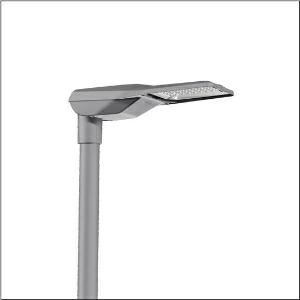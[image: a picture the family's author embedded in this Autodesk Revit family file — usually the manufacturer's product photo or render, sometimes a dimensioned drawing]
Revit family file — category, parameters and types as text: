
# Revit family: streetlight_sl_21_mini___stw1_0a_5xe6e43a08jb_3156
name_source: partatom
category: Lighting Fixtures
units: mm (PartAtom-declared; Revit-internal decimal feet)

## family parameters
Cut with Voids When Loaded = No
Host = Face
Light Source = No
Part Type = Normal
Room Calculation Point = No
Round Connector Dimension = Use Diameter
Shared = No

## types (1)
- --- (1 x LED, 13390 lm, 87.3 W, 4000K)
    Apparent Load = 87 VA
    CIE Flux Codes = 39 75 98 100 100
    Color Rendering = 70
    Color Temperature = 4000K
    Default Elevation = 1800 mm
    Description = Streetlight SL 21 mini, mast luminaire, primary light control with lens, of PMMA, primary optical cover: cover, of toughened safety glass, transparent, light distribution: STW1.0a, light emission: direct distribution, primary light characteristic: asymmetric, installation type: post-top, side-entry, LED, 3G 1.5mm², High Power LED, rated luminous flux: 13.390lm, luminous efficacy: 153lm/W, light colour: 740, colour temperature: 4000K, control: overheat protection, constant luminous flux control, time-dependent luminous flux control, flexible luminous flux parameterisation, mains connection: 230..240V, AC, 50/60Hz, connection cable pre-assembled, cable length: 10,5m, wiring characteristics: H07RN-F, start of lifetime: 87W, end of service life: 90W, reduction: 40W, luminaire housing, of diecast aluminium, powder-coated, Siteco® metallic grey (DB 702S), corrosivity category C5 mid according to DIN EN ISO 12944, please order mast flange separately, inclination adjustable: 0°, 5°, 10°, 15°, sealing non-destructively replaceable, multi-level sealing system, length: 628mm, width: 235mm, height: 110mm, mast flange for spigot size: 42mm (side-entry): 5XC10008XM4, 60/48mm (side-entry/post-top): 5XC10108XM2, 76/60mm (side-entry/post-top): 5XC10108XM1, protection rating (complete): IP66, insulation class (complete): insulation class II (safety insulation), certification: CE, ENEC, ENEC+, VDE, impact resistance: IK09, permissible operating ambient temperature for outdoor applications: -40..+50°C, standard-compliant lighting for roads and squares, packaging unit: 1 piece

Light Distribution: STW1.0a
    Height = 110 mm
    Lamp = 1 x LED
    Lamp Light Flux = 13390 lm
    Lamp Power = 87.3 W
    Lamp count = 1
    Length = 625 mm
    Luminous efficacy = 153 lm/W
    Manufacturer = Siteco
    ModVariant = No
    Model = 5XE6E43A08JB
    Number of Poles = 1
    OnlyDefault = Yes
    Power Factor = 1
    Product Name = Streetlight SL 21 mini | STW1.0a
    Product group = mast luminaire | pylon top
    ProductGroupID = 6100
    Protection Class = Protection class II
    Protection Degree = IP 66
    RLX_Detail_Level = 1
    RLX_Emergency_Light_Flux = 0 lm
    RLX_Emergency_Type = 0
    RLX_Emergency_Type_DB = No
    RlxData = <blob elided: 92273 chars, md5=975750a4>
    Socket = socket
    Standby Power = 0 W
    System Light Flux = 13390 lm
    System Power = 87 W
    Type Comments = factory setting: luminous flux: 100 % | Output Level: 100 % | 915 mA
    Type Image = l_1003519.jpg
    URL = http://relux.com
    VarID = @adj_102625
    Voltage = 0 V
    Weight = 0.00 kg
    Width = 234 mm

## geometry (parser evidence)
native form markers: Blend x4, Sweep x11
no freeform markers — native parametric forms only
